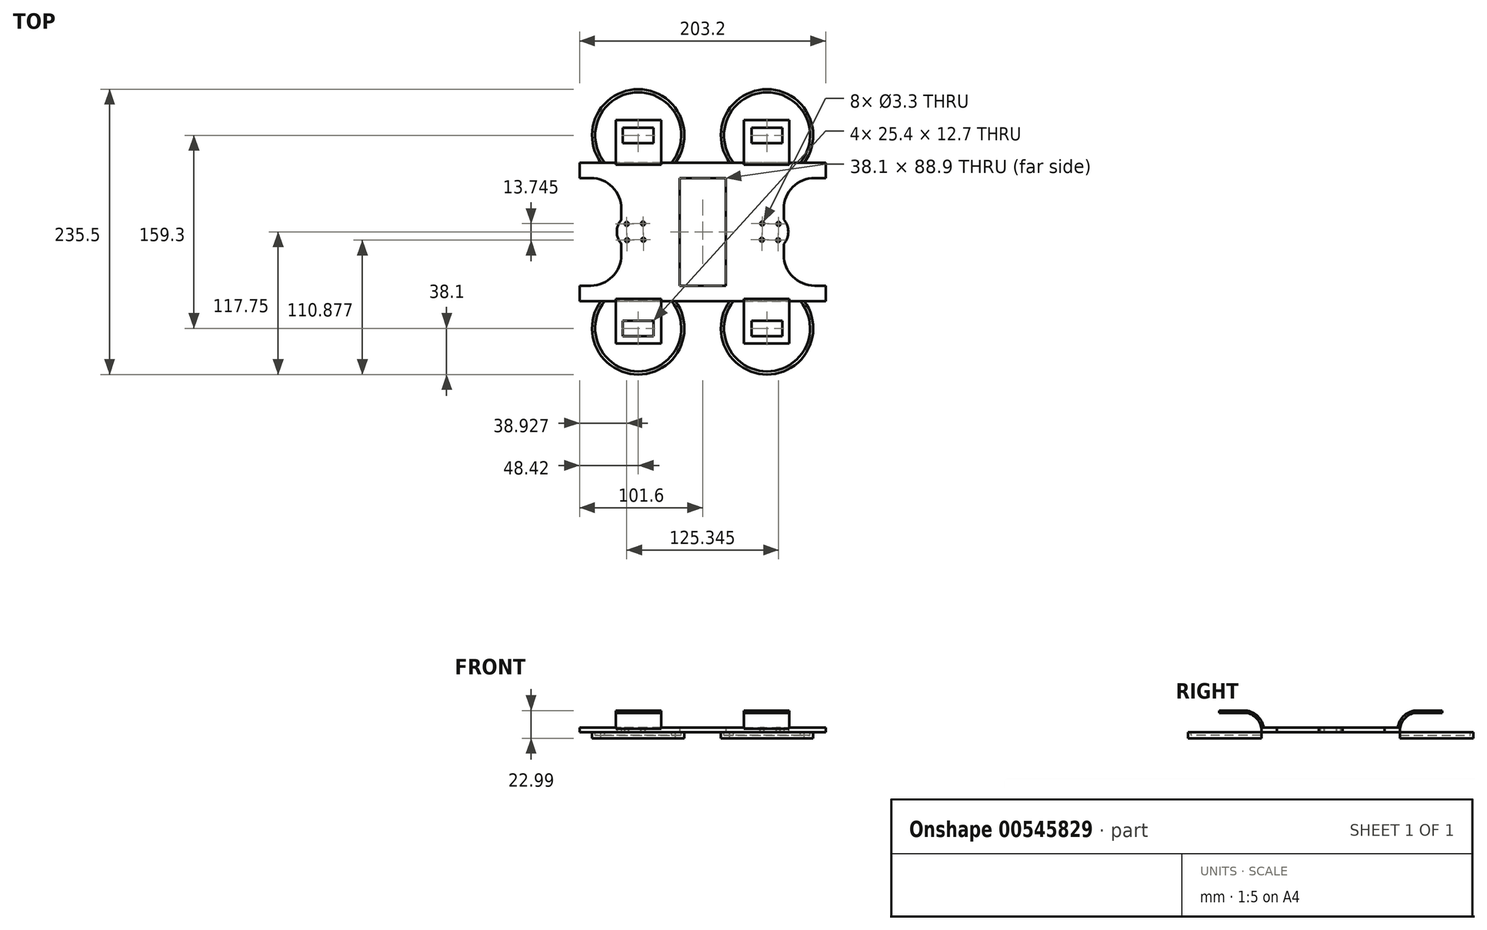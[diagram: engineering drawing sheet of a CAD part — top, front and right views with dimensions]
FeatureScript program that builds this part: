
annotation { "Feature Type Name" : "Feature", "Feature Type Description" : "" }
export const myFeature = defineFeature(function(context is Context, id is Id, definition is map)
    precondition{}
    {
        {
            var Q0;
            Q0=qCreatedBy(makeId("Top.planeOp"),FACE);
            var sketch = newSketch(context, id + "F0", { "sketchPlane" : qUnion([Q0])});
            skCircle(sketch, "E0", {"center": v(-55.8, 0) * mm, "radius": 15 * mm});
            skCircle(sketch, "E1", {"center": v(55.8, 0) * mm, "radius": 15 * mm});
            skLineSegment(sketch, "E2", {"start": v(-101.6, 57.15) * mm, "end": v(101.6, 57.15) * mm});
            skLineSegment(sketch, "E3", {"start": v(101.6, 57.15) * mm, "end": v(101.6, 44.45) * mm});
            skLineSegment(sketch, "E4", {"start": v(-101.6, 57.15) * mm, "end": v(-101.6, 44.45) * mm});
            skLineSegment(sketch, "E5", {"start": v(-101.6, -57.15) * mm, "end": v(101.6, -57.15) * mm});
            skLineSegment(sketch, "E6", {"start": v(101.6, -57.15) * mm, "end": v(101.6, -44.45) * mm});
            skLineSegment(sketch, "E7", {"start": v(-101.6, -57.15) * mm, "end": v(-101.6, -44.45) * mm});
            skCircle(sketch, "E8", {"center": v(-55.8, 0) * mm, "radius": 50.8 * mm, "construction": true});
            skCircle(sketch, "E9", {"center": v(55.8, 0) * mm, "radius": 50.8 * mm, "construction": true});
            skLineSegment(sketch, "E10.bottom", {"start": v(19.05, -44.45) * mm, "end": v(-19.05, -44.45) * mm});
            skLineSegment(sketch, "E10.top", {"start": v(19.05, 44.45) * mm, "end": v(-19.05, 44.45) * mm});
            skLineSegment(sketch, "E10.left", {"start": v(19.05, -44.45) * mm, "end": v(19.05, 44.45) * mm});
            skLineSegment(sketch, "E10.right", {"start": v(-19.05, -44.45) * mm, "end": v(-19.05, 44.45) * mm});
            skPoint(sketch, "E10.middle", {"position": v(0, 0) * mm});
            skLineSegment(sketch, "E11", {"start": v(0, 57.15) * mm, "end": v(0, -57.15) * mm, "construction": true});
            skLineSegment(sketch, "E12", {"start": v(101.6, 44.45) * mm, "end": v(67.04, 44.45) * mm});
            skLineSegment(sketch, "E13", {"start": v(67.04, 44.45) * mm, "end": v(67.04, 9.94) * mm});
            skLineSegment(sketch, "E14", {"start": v(101.6, -44.45) * mm, "end": v(67.04, -44.45) * mm});
            skLineSegment(sketch, "E15", {"start": v(67.04, -44.45) * mm, "end": v(67.04, -9.94) * mm});
            skLineSegment(sketch, "E16", {"start": v(-101.6, -44.45) * mm, "end": v(-67.04, -44.45) * mm});
            skLineSegment(sketch, "E17", {"start": v(-67.04, -44.45) * mm, "end": v(-67.04, -9.94) * mm});
            skLineSegment(sketch, "E18", {"start": v(-101.6, 44.45) * mm, "end": v(-67.04, 44.45) * mm});
            skLineSegment(sketch, "E19", {"start": v(-67.04, 44.45) * mm, "end": v(-67.04, 9.94) * mm});
            skLineSegment(sketch, "E20", {"start": v(-40.8, 0) * mm, "end": v(40.8, 0) * mm, "construction": true});
            skLineSegment(sketch, "E21", {"start": v(-111.6, -97.94) * mm, "end": v(-10, -97.94) * mm, "construction": true});
            skPoint(sketch, "E22.endSnap0", {"position": v(-60.8, -97.94) * mm});
            skLineSegment(sketch, "E23", {"start": v(-71.56, -57.15) * mm, "end": v(-71.56, -92.15) * mm});
            skLineSegment(sketch, "E24", {"start": v(-71.56, -92.15) * mm, "end": v(-34.12, -92.15) * mm});
            skLineSegment(sketch, "E25", {"start": v(-34.12, -92.15) * mm, "end": v(-34.12, -57.15) * mm});
            skLineSegment(sketch, "E26.bottom", {"start": v(-40.48, -86) * mm, "end": v(-65.88, -86) * mm});
            skLineSegment(sketch, "E26.top", {"start": v(-40.48, -73.3) * mm, "end": v(-65.88, -73.3) * mm});
            skLineSegment(sketch, "E26.left", {"start": v(-40.48, -86) * mm, "end": v(-40.48, -73.3) * mm});
            skLineSegment(sketch, "E26.right", {"start": v(-65.88, -86) * mm, "end": v(-65.88, -73.3) * mm});
            skPoint(sketch, "E26.middle", {"position": v(-53.18, -79.65) * mm});
            skPoint(sketch, "E27", {"position": v(-68.42, -79.65) * mm});
            skPoint(sketch, "E28", {"position": v(-37.94, -79.65) * mm});
            skLineSegment(sketch, "E29", {"start": v(-68.42, -79.65) * mm, "end": v(-65.88, -79.65) * mm, "construction": true});
            skLineSegment(sketch, "E30", {"start": v(-37.94, -79.65) * mm, "end": v(-40.48, -79.65) * mm, "construction": true});
            skLineSegment(sketch, "E31", {"start": v(-34.12, -57.15) * mm, "end": v(-34.12, -55.36) * mm});
            skLineSegment(sketch, "E32", {"start": v(-34.12, -55.36) * mm, "end": v(-71.56, -55.36) * mm});
            skLineSegment(sketch, "E33", {"start": v(-71.56, -55.36) * mm, "end": v(-71.56, -57.15) * mm});
            skLineSegment(sketch, "E34", {"start": v(-60.8, -73.3) * mm, "end": v(-60.8, -86) * mm, "construction": true});
            skLineSegment(sketch, "E35", {"start": v(-60.8, -79.65) * mm, "end": v(-60.8, -97.94) * mm, "construction": true});
            skPoint(sketch, "E36", {"position": v(-60.8, -79.65) * mm});
            skSolve(sketch);
        }
        {
            var Q0;
            Q0=makeQuery(id+"F0.imprint","IMPRINT",FACE,{"disambiguationData":[TD([[makeQuery(id+"F0.imprint","IMPRINT",EDGE,{"derivedFrom":sQuery(id+"F0.wireOp",EDGE,"E2")}),-1.0]])]});
            var Q1;
            {var subQ0=sQuery(id+"F0.wireOp",EDGE,"E0");var subQ1=makeQuery(id+"F0.imprint","INTERSECT",VERTEX,{"derivedFrom":[subQ0,sQuery(id+"F0.wireOp",EDGE,"E17")]});Q1=makeQuery(id+"F0.imprint","IMPRINT",FACE,{"disambiguationData":[TD([[makeQuery(id+"F0.imprint","IMPRINT",EDGE,{"disambiguationData":[TD([[subQ1,1.0]])],"derivedFrom":subQ0}),1.0]])]});}
            var Q2;
            {var subQ0=sQuery(id+"F0.wireOp",EDGE,"E1");var subQ1=makeQuery(id+"F0.imprint","INTERSECT",VERTEX,{"derivedFrom":[subQ0,sQuery(id+"F0.wireOp",EDGE,"E13")]});Q2=makeQuery(id+"F0.imprint","IMPRINT",FACE,{"disambiguationData":[TD([[makeQuery(id+"F0.imprint","IMPRINT",EDGE,{"disambiguationData":[TD([[subQ1,-1.0]])],"derivedFrom":subQ0}),1.0]])]});}
            extrude(context, id + "F1", {"entities" : qUnion([Q0, Q1, Q2]), "depth" : 3.8 * mm, "offsetDistance" : 25.4 * mm, "symmetric" : true});
        }
        {
            var Q0;
            Q0=makeQuery(id+"F1.opExtrude","SWEPT_EDGE",EDGE,{"disambiguationData":[OSD([sQuery(id+"F0.wireOp",EDGE,"E18"),sQuery(id+"F0.wireOp",EDGE,"E19")])]});
            var Q1;
            Q1=makeQuery(id+"F1.opExtrude","SWEPT_EDGE",EDGE,{"disambiguationData":[OSD([sQuery(id+"F0.wireOp",EDGE,"E16"),sQuery(id+"F0.wireOp",EDGE,"E17")])]});
            var Q2;
            Q2=makeQuery(id+"F1.opExtrude","SWEPT_EDGE",EDGE,{"disambiguationData":[OSD([sQuery(id+"F0.wireOp",EDGE,"E12"),sQuery(id+"F0.wireOp",EDGE,"E13")])]});
            var Q3;
            Q3=makeQuery(id+"F1.opExtrude","SWEPT_EDGE",EDGE,{"disambiguationData":[OSD([sQuery(id+"F0.wireOp",EDGE,"E14"),sQuery(id+"F0.wireOp",EDGE,"E15")])]});
            fillet(context, id + "F2", {"entities" : qUnion([Q0, Q1, Q2, Q3]), "radius" : 25.4 * mm, "tangentPropagation" : true, "allowEdgeOverflow" : false});
        }
        {
            var Q0;
            {var subQ1=sQuery(id+"F0.wireOp",EDGE,"E23");Q0=makeQuery(id+"F0.imprint","IMPRINT",FACE,{"disambiguationData":[TD([[makeQuery(id+"F0.imprint","IMPRINT",EDGE,{"derivedFrom":subQ1}),1.0]])]});}
            var Q1;
            {var subQ2=sQuery(id+"F0.wireOp",EDGE,"E31");Q1=makeQuery(id+"F0.imprint","IMPRINT",FACE,{"disambiguationData":[TD([[makeQuery(id+"F0.imprint","IMPRINT",EDGE,{"derivedFrom":subQ2}),1.0]])]});}
            extrude(context, id + "F3", {"entities" : qUnion([Q0, Q1]), "operationType" : NewBodyOperationType.ADD, "depth" : 16 * mm, "offsetDistance" : 25.4 * mm, "hasSecondDirection" : true, "secondDirectionOppositeDirection" : true, "secondDirectionDepth" : 1.9 * mm});
        }
        {
            var Q0;
            Q0=makeQuery(id+"F3.opExtrude","CAP_EDGE",EDGE,{"disambiguationData":[OSD([sQuery(id+"F0.wireOp",EDGE,"E5")])],"isStart":false});
            var Q1;
            Q1=makeQuery(id+"F3.opExtrude","CAP_EDGE",EDGE,{"disambiguationData":[OSD([sQuery(id+"F0.wireOp",EDGE,"E32")])],"isStart":false});
            fillet(context, id + "F4", {"entities" : qUnion([Q0, Q1]), "radius" : 16.56 * mm, "tangentPropagation" : true, "allowEdgeOverflow" : false});
        }
        {
            var Q0;
            Q0=makeQuery(id+"F3.opExtrude","SWEPT_FACE",FACE,{"disambiguationData":[OSD([sQuery(id+"F0.wireOp",EDGE,"E23")])]});
            var sketch = newSketch(context, id + "F5", { "sketchPlane" : qUnion([Q0])});
            skLineSegment(sketch, "E37", {"start": v(92.15, 14.09) * mm, "end": v(92.15, -1.9) * mm});
            skLineSegment(sketch, "E38", {"start": v(92.15, -1.9) * mm, "end": v(57.15, -1.9) * mm});
            skLineSegment(sketch, "E39", {"start": v(92.15, 14.09) * mm, "end": v(71.73, 14.09) * mm});
            skArc(sketch, "E40", {"start": v(71.73, 14.09) * mm, "mid": v(60.91, 9.31) * mm, "end": v(57.15, -1.9) * mm});
            skSolve(sketch);
        }
        {
            var Q0;
            Q0=makeQuery(id+"F5.imprint","IMPRINT",FACE,{"disambiguationData":[TD([[makeQuery(id+"F5.imprint","IMPRINT",EDGE,{"derivedFrom":sQuery(id+"F5.wireOp",EDGE,"E37")}),-1.0]])]});
            extrude(context, id + "F6", {"entities" : qUnion([Q0]), "operationType" : NewBodyOperationType.REMOVE, "oppositeDirection" : true, "depth" : 38.1 * mm, "offsetDistance" : 25.4 * mm});
        }
        {
            var Q0;
            Q0=makeQuery(id+"F1.opExtrude","SWEPT_BODY",BODY,{"disambiguationData":[OSD([sQuery(id+"F0.wireOp",EDGE,"E0"),sQuery(id+"F0.wireOp",EDGE,"E1"),sQuery(id+"F0.wireOp",EDGE,"E2"),sQuery(id+"F0.wireOp",EDGE,"E3"),sQuery(id+"F0.wireOp",EDGE,"E4"),sQuery(id+"F0.wireOp",EDGE,"E5"),sQuery(id+"F0.wireOp",EDGE,"E6"),sQuery(id+"F0.wireOp",EDGE,"E7"),sQuery(id+"F0.wireOp",EDGE,"E10.bottom"),sQuery(id+"F0.wireOp",EDGE,"E10.top"),sQuery(id+"F0.wireOp",EDGE,"E10.left"),sQuery(id+"F0.wireOp",EDGE,"E10.right"),sQuery(id+"F0.wireOp",EDGE,"E12"),sQuery(id+"F0.wireOp",EDGE,"E13"),sQuery(id+"F0.wireOp",EDGE,"E14"),sQuery(id+"F0.wireOp",EDGE,"E15"),sQuery(id+"F0.wireOp",EDGE,"E16"),sQuery(id+"F0.wireOp",EDGE,"E17"),sQuery(id+"F0.wireOp",EDGE,"E18"),sQuery(id+"F0.wireOp",EDGE,"E19")])]});
            var Q1;
            Q1=qCreatedBy(makeId("Right.planeOp"),FACE);
            mirror(context, id + "F7", {"operationType" : NewBodyOperationType.ADD, "entities" : qUnion([Q0]), "mirrorPlane" : qUnion([Q1])});
        }
        {
            var Q0;
            Q0=makeQuery(id+"F1.opExtrude","SWEPT_BODY",BODY,{"disambiguationData":[OSD([sQuery(id+"F0.wireOp",EDGE,"E0"),sQuery(id+"F0.wireOp",EDGE,"E1"),sQuery(id+"F0.wireOp",EDGE,"E2"),sQuery(id+"F0.wireOp",EDGE,"E3"),sQuery(id+"F0.wireOp",EDGE,"E4"),sQuery(id+"F0.wireOp",EDGE,"E5"),sQuery(id+"F0.wireOp",EDGE,"E6"),sQuery(id+"F0.wireOp",EDGE,"E7"),sQuery(id+"F0.wireOp",EDGE,"E10.bottom"),sQuery(id+"F0.wireOp",EDGE,"E10.top"),sQuery(id+"F0.wireOp",EDGE,"E10.left"),sQuery(id+"F0.wireOp",EDGE,"E10.right"),sQuery(id+"F0.wireOp",EDGE,"E12"),sQuery(id+"F0.wireOp",EDGE,"E13"),sQuery(id+"F0.wireOp",EDGE,"E14"),sQuery(id+"F0.wireOp",EDGE,"E15"),sQuery(id+"F0.wireOp",EDGE,"E16"),sQuery(id+"F0.wireOp",EDGE,"E17"),sQuery(id+"F0.wireOp",EDGE,"E18"),sQuery(id+"F0.wireOp",EDGE,"E19")])]});
            var Q1;
            Q1=qCreatedBy(makeId("Front.planeOp"),FACE);
            mirror(context, id + "F8", {"operationType" : NewBodyOperationType.ADD, "entities" : qUnion([Q0]), "mirrorPlane" : qUnion([Q1])});
        }
        {
            var Q0;
            Q0=makeQuery(id+"F1.opExtrude","CAP_FACE",FACE,{"disambiguationData":[OSD([sQuery(id+"F0.wireOp",EDGE,"E0"),sQuery(id+"F0.wireOp",EDGE,"E1"),sQuery(id+"F0.wireOp",EDGE,"E2"),sQuery(id+"F0.wireOp",EDGE,"E3"),sQuery(id+"F0.wireOp",EDGE,"E4"),sQuery(id+"F0.wireOp",EDGE,"E5"),sQuery(id+"F0.wireOp",EDGE,"E6"),sQuery(id+"F0.wireOp",EDGE,"E7"),sQuery(id+"F0.wireOp",EDGE,"E10.bottom"),sQuery(id+"F0.wireOp",EDGE,"E10.top"),sQuery(id+"F0.wireOp",EDGE,"E10.left"),sQuery(id+"F0.wireOp",EDGE,"E10.right"),sQuery(id+"F0.wireOp",EDGE,"E12"),sQuery(id+"F0.wireOp",EDGE,"E13"),sQuery(id+"F0.wireOp",EDGE,"E14"),sQuery(id+"F0.wireOp",EDGE,"E15"),sQuery(id+"F0.wireOp",EDGE,"E16"),sQuery(id+"F0.wireOp",EDGE,"E17"),sQuery(id+"F0.wireOp",EDGE,"E18"),sQuery(id+"F0.wireOp",EDGE,"E19")])],"isStart":false});
            var sketch = newSketch(context, id + "F9", { "sketchPlane" : qUnion([Q0])});
            skPoint(sketch, "E41", {"position": v(-55.8, 0) * mm});
            skCircle(sketch, "E42", {"center": v(-55.8, 0) * mm, "radius": 9.5 * mm, "construction": true});
            skCircle(sketch, "E43", {"center": v(-55.8, 0) * mm, "radius": 8 * mm, "construction": true});
            skLineSegment(sketch, "E44", {"start": v(-62.67, 6.56) * mm, "end": v(-55.8, 0) * mm, "construction": true});
            skLineSegment(sketch, "E45", {"start": v(-55.8, 0) * mm, "end": v(-62.36, -6.87) * mm, "construction": true});
            skLineSegment(sketch, "E46", {"start": v(-55.8, 0) * mm, "end": v(-48.93, -6.56) * mm, "construction": true});
            skLineSegment(sketch, "E47", {"start": v(-55.8, 0) * mm, "end": v(-49.24, 6.87) * mm, "construction": true});
            skPoint(sketch, "E48", {"position": v(-49.24, 6.87) * mm});
            skPoint(sketch, "E49", {"position": v(-48.93, -6.56) * mm});
            skPoint(sketch, "E50", {"position": v(-62.36, -6.87) * mm});
            skPoint(sketch, "E51", {"position": v(-62.67, 6.56) * mm});
            skPoint(sketch, "E52.MirrorP", {"position": v(55.8, 0) * mm});
            skPoint(sketch, "E53.MirrorP", {"position": v(48.93, -6.56) * mm});
            skPoint(sketch, "E54.MirrorP", {"position": v(62.36, -6.87) * mm});
            skPoint(sketch, "E55.MirrorP", {"position": v(49.24, 6.87) * mm});
            skPoint(sketch, "E56.MirrorP", {"position": v(62.67, 6.56) * mm});
            skCircle(sketch, "E57", {"center": v(-55.8, 0) * mm, "radius": 14 * mm});
            skSolve(sketch);
        }
        {
            var Q0;
            Q0=sQuery(id+"F9.wireOp",VERTEX,"E51");
            var Q1;
            Q1=sQuery(id+"F9.wireOp",VERTEX,"E50");
            var Q2;
            Q2=sQuery(id+"F9.wireOp",VERTEX,"E49");
            var Q3;
            Q3=sQuery(id+"F9.wireOp",VERTEX,"E48");
            var Q4;
            Q4=sQuery(id+"F9.wireOp",VERTEX,"E55.MirrorP");
            var Q5;
            Q5=sQuery(id+"F9.wireOp",VERTEX,"E56.MirrorP");
            var Q6;
            Q6=sQuery(id+"F9.wireOp",VERTEX,"E54.MirrorP");
            var Q7;
            Q7=sQuery(id+"F9.wireOp",VERTEX,"E53.MirrorP");
            var Q8;
            Q8=makeQuery(id+"F1.opExtrude","SWEPT_BODY",BODY,{"disambiguationData":[OSD([sQuery(id+"F0.wireOp",EDGE,"E0"),sQuery(id+"F0.wireOp",EDGE,"E1"),sQuery(id+"F0.wireOp",EDGE,"E2"),sQuery(id+"F0.wireOp",EDGE,"E3"),sQuery(id+"F0.wireOp",EDGE,"E4"),sQuery(id+"F0.wireOp",EDGE,"E5"),sQuery(id+"F0.wireOp",EDGE,"E6"),sQuery(id+"F0.wireOp",EDGE,"E7"),sQuery(id+"F0.wireOp",EDGE,"E10.bottom"),sQuery(id+"F0.wireOp",EDGE,"E10.top"),sQuery(id+"F0.wireOp",EDGE,"E10.left"),sQuery(id+"F0.wireOp",EDGE,"E10.right"),sQuery(id+"F0.wireOp",EDGE,"E12"),sQuery(id+"F0.wireOp",EDGE,"E13"),sQuery(id+"F0.wireOp",EDGE,"E14"),sQuery(id+"F0.wireOp",EDGE,"E15"),sQuery(id+"F0.wireOp",EDGE,"E16"),sQuery(id+"F0.wireOp",EDGE,"E17"),sQuery(id+"F0.wireOp",EDGE,"E18"),sQuery(id+"F0.wireOp",EDGE,"E19")])]});
            hole(context, id + "F10", {"style" : HoleStyle.SIMPLE, "endStyle" : HoleEndStyle.THROUGH, "standardTappedOrClearance" : lookupTablePath({ "standard" : "ISO", "fit" : "Normal", "size" : "M3", "type" : "Clearance" }), "standardBlindInLast" : lookupTablePath({ "fit" : "Standard", "standard" : "ISO", "size" : "M3", "type" : "Clearance" }), "holeDiameter" : 3.3 * mm, "isTappedThrough" : true, "tappedDepth" : 12.7 * mm, "tapClearance" : 3, "locations" : qUnion([Q0, Q1, Q2, Q3, Q4, Q5, Q6, Q7]), "scope" : qUnion([Q8])});
        }
        {
            var Q0;
            {var subQ0=sQuery(id+"F0.wireOp",EDGE,"E5");Q0=makeQuery(id+"F3.boolean.opBoolean","MERGE",FACE,{"derivedFrom":[makeQuery(id+"F1.opExtrude","CAP_FACE",FACE,{"disambiguationData":[OSD([sQuery(id+"F0.wireOp",EDGE,"E0"),sQuery(id+"F0.wireOp",EDGE,"E1"),sQuery(id+"F0.wireOp",EDGE,"E2"),sQuery(id+"F0.wireOp",EDGE,"E3"),sQuery(id+"F0.wireOp",EDGE,"E4"),subQ0,sQuery(id+"F0.wireOp",EDGE,"E6"),sQuery(id+"F0.wireOp",EDGE,"E7"),sQuery(id+"F0.wireOp",EDGE,"E10.bottom"),sQuery(id+"F0.wireOp",EDGE,"E10.top"),sQuery(id+"F0.wireOp",EDGE,"E10.left"),sQuery(id+"F0.wireOp",EDGE,"E10.right"),sQuery(id+"F0.wireOp",EDGE,"E12"),sQuery(id+"F0.wireOp",EDGE,"E13"),sQuery(id+"F0.wireOp",EDGE,"E14"),sQuery(id+"F0.wireOp",EDGE,"E15"),sQuery(id+"F0.wireOp",EDGE,"E16"),sQuery(id+"F0.wireOp",EDGE,"E17"),sQuery(id+"F0.wireOp",EDGE,"E18"),sQuery(id+"F0.wireOp",EDGE,"E19")])],"isStart":true}),makeQuery(id+"F3.opExtrude","CAP_FACE",FACE,{"disambiguationData":[OSD([subQ0,sQuery(id+"F0.wireOp",EDGE,"E23"),sQuery(id+"F0.wireOp",EDGE,"E24"),sQuery(id+"F0.wireOp",EDGE,"E25"),sQuery(id+"F0.wireOp",EDGE,"E26.bottom"),sQuery(id+"F0.wireOp",EDGE,"E26.top"),sQuery(id+"F0.wireOp",EDGE,"E26.left"),sQuery(id+"F0.wireOp",EDGE,"E26.right")])],"isStart":true})]});}
            var sketch = newSketch(context, id + "F11", { "sketchPlane" : qUnion([Q0])});
            skLineSegment(sketch, "E58", {"start": v(-53.18, 57.15) * mm, "end": v(-53.18, 79.65) * mm, "construction": true});
            skCircle(sketch, "E59", {"center": v(-53.18, 79.65) * mm, "radius": 16.23 * mm, "construction": true});
            skLineSegment(sketch, "E60", {"start": v(-53.18, 79.65) * mm, "end": v(-41.7, 91.13) * mm, "construction": true});
            skCircle(sketch, "E61", {"center": v(-53.18, 79.65) * mm, "radius": 35.56 * mm});
            skLineSegment(sketch, "E62", {"start": v(-41.7, 91.13) * mm, "end": v(-28.04, 104.8) * mm, "construction": true});
            skLineSegment(sketch, "E63", {"start": v(-53.18, 79.65) * mm, "end": v(-36.95, 79.65) * mm, "construction": true});
            skLineSegment(sketch, "E64", {"start": v(-67.3, 137.04) * mm, "end": v(11.22, 72.56) * mm, "construction": true});
            skLineSegment(sketch, "E65", {"start": v(-53.18, 79.65) * mm, "end": v(-78.32, 54.5) * mm, "construction": true});
            skCircle(sketch, "E66", {"center": v(-53.18, 79.65) * mm, "radius": 38.1 * mm});
            skSolve(sketch);
        }
        {
            var Q0;
            {var subQ0=sQuery(id+"F11.wireOp",EDGE,"E61");var subQ1=sQuery(id+"F0.wireOp",EDGE,"E33");var subQ2=sQuery(id+"F0.wireOp",EDGE,"E23");var subQ3=sQuery(id+"F0.wireOp",EDGE,"E5");var subQ4=makeQuery(id+"F6.boolean.opBoolean","MERGE",EDGE,{"derivedFrom":[makeQuery(id+"F1.opExtrude","CAP_EDGE",EDGE,{"disambiguationData":[OSD([subQ3]),TDD([makeQuery(id+"F0.imprint","IMPRINT",EDGE,{"disambiguationData":[TD([[makeQuery(id+"F0.imprint","INTERSECT",VERTEX,{"derivedFrom":[subQ3,sQuery(id+"F0.wireOp",EDGE,"E7")]}),-1.0]])],"derivedFrom":subQ3})])],"isStart":true}),makeQuery(id+"F1.opExtrude","CAP_EDGE",EDGE,{"disambiguationData":[OSD([subQ3]),TDD([makeQuery(id+"F0.imprint","IMPRINT",EDGE,{"disambiguationData":[TD([[makeQuery(id+"F0.imprint","INTERSECT",VERTEX,{"derivedFrom":[subQ3,sQuery(id+"F0.wireOp",EDGE,"E6")]}),1.0]])],"derivedFrom":subQ3})])],"isStart":true}),makeQuery(id+"F6.opExtrude","SWEPT_EDGE",EDGE,{"disambiguationData":[OSD([subQ3,subQ2,subQ1,sQuery(id+"F5.wireOp",EDGE,"E38"),sQuery(id+"F5.wireOp",EDGE,"E40")])]})]});var subQ5=makeQuery(id+"F11.imprint","INTERSECT",VERTEX,{"disambiguationData":[OD(0.0)],"derivedFrom":[subQ4,subQ0]});Q0=makeQuery(id+"F11.imprint","IMPRINT",FACE,{"disambiguationData":[TD([[makeQuery(id+"F11.imprint","IMPRINT",EDGE,{"disambiguationData":[TD([[subQ5,-1.0]])],"derivedFrom":subQ0}),-1.0]])]});}
            var Q1;
            {var subQ0=sQuery(id+"F11.wireOp",EDGE,"E61");var subQ1=sQuery(id+"F0.wireOp",EDGE,"E33");var subQ2=sQuery(id+"F0.wireOp",EDGE,"E23");var subQ3=sQuery(id+"F0.wireOp",EDGE,"E5");var subQ4=makeQuery(id+"F6.boolean.opBoolean","MERGE",EDGE,{"derivedFrom":[makeQuery(id+"F1.opExtrude","CAP_EDGE",EDGE,{"disambiguationData":[OSD([subQ3]),TDD([makeQuery(id+"F0.imprint","IMPRINT",EDGE,{"disambiguationData":[TD([[makeQuery(id+"F0.imprint","INTERSECT",VERTEX,{"derivedFrom":[subQ3,sQuery(id+"F0.wireOp",EDGE,"E7")]}),-1.0]])],"derivedFrom":subQ3})])],"isStart":true}),makeQuery(id+"F1.opExtrude","CAP_EDGE",EDGE,{"disambiguationData":[OSD([subQ3]),TDD([makeQuery(id+"F0.imprint","IMPRINT",EDGE,{"disambiguationData":[TD([[makeQuery(id+"F0.imprint","INTERSECT",VERTEX,{"derivedFrom":[subQ3,sQuery(id+"F0.wireOp",EDGE,"E6")]}),1.0]])],"derivedFrom":subQ3})])],"isStart":true}),makeQuery(id+"F6.opExtrude","SWEPT_EDGE",EDGE,{"disambiguationData":[OSD([subQ3,subQ2,subQ1,sQuery(id+"F5.wireOp",EDGE,"E38"),sQuery(id+"F5.wireOp",EDGE,"E40")])]})]});var subQ5=makeQuery(id+"F11.imprint","INTERSECT",VERTEX,{"disambiguationData":[OD(0.0)],"derivedFrom":[subQ4,subQ0]});Q1=makeQuery(id+"F11.imprint","IMPRINT",FACE,{"disambiguationData":[TD([[makeQuery(id+"F11.imprint","IMPRINT",EDGE,{"disambiguationData":[TD([[subQ5,-1.0]])],"derivedFrom":subQ0}),1.0]])]});}
            extrude(context, id + "F12", {"entities" : qUnion([Q0, Q1]), "depth" : 5.08 * mm, "offsetDistance" : 25.4 * mm});
        }
        {
            var Q0;
            {var subQ0=sQuery(id+"F11.wireOp",EDGE,"E61");var subQ1=sQuery(id+"F0.wireOp",EDGE,"E33");var subQ2=sQuery(id+"F0.wireOp",EDGE,"E23");var subQ3=sQuery(id+"F0.wireOp",EDGE,"E5");var subQ4=makeQuery(id+"F6.boolean.opBoolean","MERGE",EDGE,{"derivedFrom":[makeQuery(id+"F1.opExtrude","CAP_EDGE",EDGE,{"disambiguationData":[OSD([subQ3]),TDD([makeQuery(id+"F0.imprint","IMPRINT",EDGE,{"disambiguationData":[TD([[makeQuery(id+"F0.imprint","INTERSECT",VERTEX,{"derivedFrom":[subQ3,sQuery(id+"F0.wireOp",EDGE,"E7")]}),-1.0]])],"derivedFrom":subQ3})])],"isStart":true}),makeQuery(id+"F1.opExtrude","CAP_EDGE",EDGE,{"disambiguationData":[OSD([subQ3]),TDD([makeQuery(id+"F0.imprint","IMPRINT",EDGE,{"disambiguationData":[TD([[makeQuery(id+"F0.imprint","INTERSECT",VERTEX,{"derivedFrom":[subQ3,sQuery(id+"F0.wireOp",EDGE,"E6")]}),1.0]])],"derivedFrom":subQ3})])],"isStart":true}),makeQuery(id+"F6.opExtrude","SWEPT_EDGE",EDGE,{"disambiguationData":[OSD([subQ3,subQ2,subQ1,sQuery(id+"F5.wireOp",EDGE,"E38"),sQuery(id+"F5.wireOp",EDGE,"E40")])]})]});var subQ5=makeQuery(id+"F11.imprint","INTERSECT",VERTEX,{"disambiguationData":[OD(0.0)],"derivedFrom":[subQ4,subQ0]});Q0=makeQuery(id+"F11.imprint","IMPRINT",FACE,{"disambiguationData":[TD([[makeQuery(id+"F11.imprint","IMPRINT",EDGE,{"disambiguationData":[TD([[subQ5,-1.0]])],"derivedFrom":subQ0}),1.0]])]});}
            extrude(context, id + "F13", {"entities" : qUnion([Q0]), "depth" : 2.54 * mm, "offsetDistance" : 25.4 * mm});
        }
        {
            var Q0;
            Q0=makeQuery(id+"F13.opExtrude","SWEPT_BODY",BODY,{"disambiguationData":[OSD([sQuery(id+"F0.wireOp",EDGE,"E5"),sQuery(id+"F0.wireOp",EDGE,"E23"),sQuery(id+"F5.wireOp",EDGE,"E38"),sQuery(id+"F5.wireOp",EDGE,"E40"),sQuery(id+"F11.wireOp",EDGE,"E61")])]});
            var Q1;
            Q1=makeQuery(id+"F12.opExtrude","SWEPT_BODY",BODY,{"disambiguationData":[OSD([sQuery(id+"F0.wireOp",EDGE,"E5"),sQuery(id+"F0.wireOp",EDGE,"E23"),sQuery(id+"F5.wireOp",EDGE,"E38"),sQuery(id+"F5.wireOp",EDGE,"E40"),sQuery(id+"F11.wireOp",EDGE,"E66")])]});
            booleanBodies(context, id + "F14", {"operationType" : BooleanOperationType.SUBTRACTION, "tools" : qUnion([Q0]), "targets" : qUnion([Q1])});
        }
        {
            var Q0;
            Q0=makeQuery(id+"F12.opExtrude","SWEPT_BODY",BODY,{"disambiguationData":[OSD([sQuery(id+"F0.wireOp",EDGE,"E5"),sQuery(id+"F0.wireOp",EDGE,"E23"),sQuery(id+"F5.wireOp",EDGE,"E38"),sQuery(id+"F5.wireOp",EDGE,"E40"),sQuery(id+"F11.wireOp",EDGE,"E66")])]});
            var Q1;
            Q1=qCreatedBy(makeId("Front.planeOp"),FACE);
            mirror(context, id + "F15", {"entities" : qUnion([Q0]), "mirrorPlane" : qUnion([Q1])});
        }
        {
            var Q0;
            Q0=makeQuery(id+"F12.opExtrude","SWEPT_BODY",BODY,{"disambiguationData":[OSD([sQuery(id+"F0.wireOp",EDGE,"E5"),sQuery(id+"F0.wireOp",EDGE,"E23"),sQuery(id+"F5.wireOp",EDGE,"E38"),sQuery(id+"F5.wireOp",EDGE,"E40"),sQuery(id+"F11.wireOp",EDGE,"E66")])]});
            var Q1;
            Q1=makeQuery(id+"F15.opPattern","COPY",BODY,{"derivedFrom":makeQuery(id+"F12.opExtrude","SWEPT_BODY",BODY,{"disambiguationData":[OSD([sQuery(id+"F0.wireOp",EDGE,"E5"),sQuery(id+"F0.wireOp",EDGE,"E23"),sQuery(id+"F5.wireOp",EDGE,"E38"),sQuery(id+"F5.wireOp",EDGE,"E40"),sQuery(id+"F11.wireOp",EDGE,"E66")])]}),"instanceName":"1"});
            var Q2;
            Q2=qCreatedBy(makeId("Right.planeOp"),FACE);
            mirror(context, id + "F16", {"operationType" : NewBodyOperationType.ADD, "entities" : qUnion([Q0, Q1]), "mirrorPlane" : qUnion([Q2])});
        }
    });
